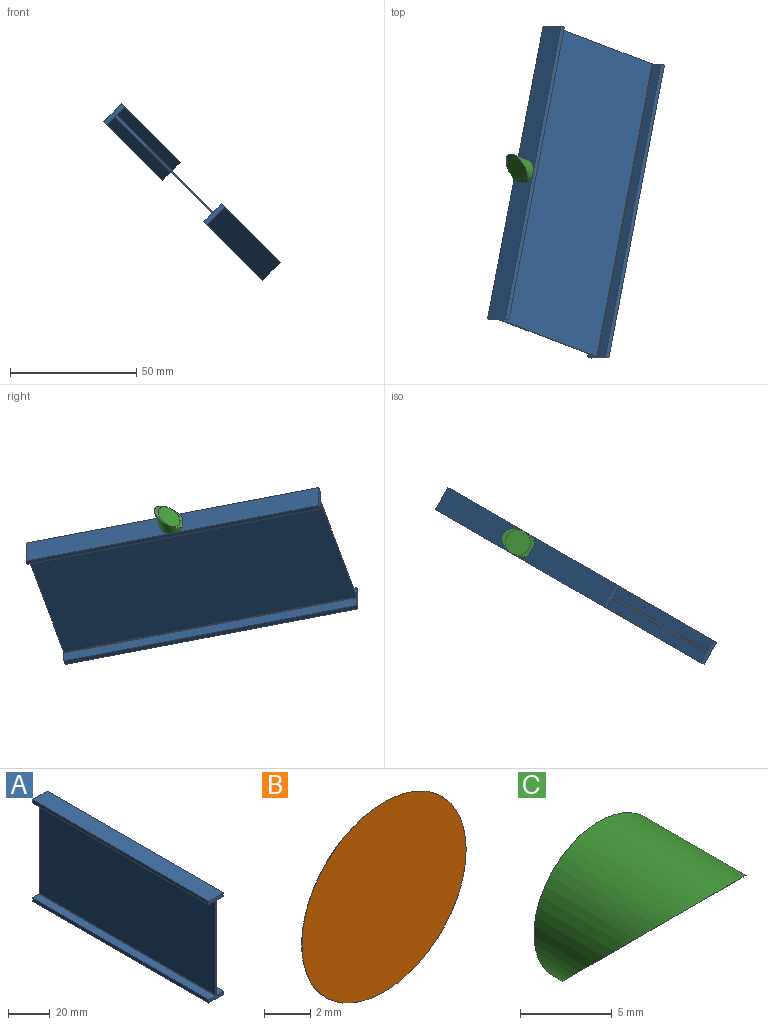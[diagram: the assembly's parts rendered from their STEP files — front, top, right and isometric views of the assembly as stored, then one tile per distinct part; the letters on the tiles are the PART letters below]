
ASSEMBLY  parts=3 mates=2
PART A: 18 faces, bbox 10x120x60 mm
  f0: cylinder r=0.24mm len=120mm, axis (0,1,0), area 45.2mm2, adj f1,f15,f16,f17
  f1: plane 120x4.41mm, normal (0,0,1), area 528.6mm2, adj f0,f2,f16,f17
  f2: plane 120x2mm, normal (-1,0,0), area 240mm2, adj f1,f3,f16,f17
  f3: plane 120x10mm, normal (0,0,-1), area 1200mm2, adj f2,f4,f16,f17
  f4: plane 120x2mm, normal (1,0,0), area 240mm2, adj f3,f5,f16,f17
  f5: plane 120x4.41mm, normal (0,0,1), area 528.6mm2, adj f4,f6,f16,f17
  f6: cylinder r=0.24mm len=120mm, axis (0,1,0), area 45.2mm2, adj f5,f7,f16,f17
  f7: plane 120x55.52mm, normal (1,0,0), area 6662.4mm2, adj f6,f8,f16,f17
  f8: cylinder r=0.24mm len=120mm, axis (0,1,0), area 45.2mm2, adj f7,f9,f16,f17
  f9: plane 120x4.41mm, normal (0,0,-1), area 528.6mm2, adj f8,f10,f16,f17
  f10: plane 120x2mm, normal (1,0,0), area 240mm2, adj f9,f11,f16,f17
  f11: plane 120x10mm, normal (0,0,1), area 1200mm2, adj f10,f12,f16,f17
  f12: plane 120x2mm, normal (-1,0,0), area 240mm2, adj f11,f13,f16,f17
  f13: plane 120x4.41mm, normal (0,0,-1), area 528.6mm2, adj f12,f14,f16,f17
  f14: cylinder r=0.24mm len=120mm, axis (0,1,0), area 45.2mm2, adj f13,f15,f16,f17
  f15: plane 120x55.52mm, normal (-1,0,0), area 6662.4mm2, adj f0,f14,f16,f17
  f16: plane 60x10mm, normal (0,-1,0), area 79.8mm2, adj f0,f1,f2,f3,f4,f5,f6,f7
  f17: plane 60x10mm, normal (0,1,0), area 79.8mm2, adj f0,f1,f2,f3,f4,f5,f6,f7
PART B: 3 faces, bbox 10x0x10 mm
  f0: cylinder r=5mm len=10mm, axis (0,-1,0), area 0.3mm2, adj f1,f2
  f1: plane 10x10mm, normal (0,1,0), area 78.5mm2, adj f0
  f2: plane 10x10mm, normal (0,-1,0), area 78.5mm2, adj f0
PART C: 3 faces, bbox 10x9.3x9.2 mm
  f0: cylinder r=5mm len=10mm, axis (0,1,0), area 136.1mm2, adj f1,f2
  f1: plane 10x9.24mm, normal (0,-0.71,-0.71), area 107.2mm2, adj f0,f2
  f2: plane 10x9.24mm, normal (0,1,0), area 75.8mm2, adj f0,f1
PLACE A rot(axis=(-0.38,0.12,0.92),174.3deg) t=(141.42,-50.05,-154.29)mm fixed
PLACE B rot(axis=(-0.77,-0.55,-0.32),73.7deg) t=(-31.83,77.79,18.46)mm
PLACE C rot(axis=(-0.89,-0.28,-0.37),111.6deg) t=(-28.85,76.5,15.48)mm
MATE fastened B.f0 <-> C.f1  axis (0.61,0.5,-0.61) through (-31.83,77.79,18.46)mm
MATE fastened C.f0 <-> A.f11  axis (0.68,-0.26,-0.68) through (-28.85,76.5,15.48)mm
